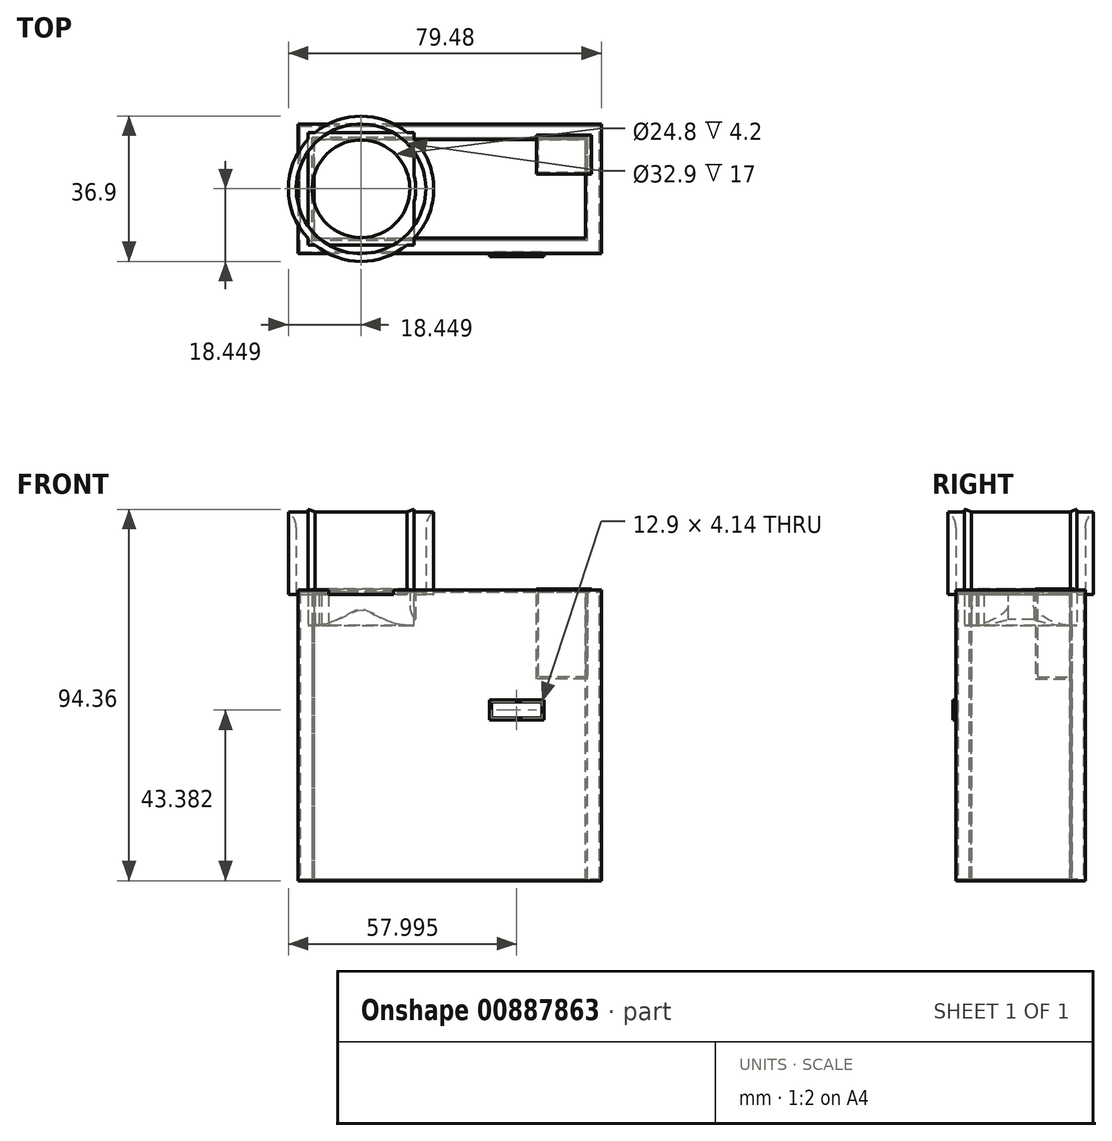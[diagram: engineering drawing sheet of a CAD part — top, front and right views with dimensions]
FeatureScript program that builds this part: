
annotation { "Feature Type Name" : "Feature", "Feature Type Description" : "" }
export const myFeature = defineFeature(function(context is Context, id is Id, definition is map)
    precondition{}
    {
        {
            var Q0;
            Q0=qCreatedBy(makeId("Front.planeOp"),FACE);
            var sketch = newSketch(context, id + "F0", { "sketchPlane" : qUnion([Q0])});
            skLineSegment(sketch, "E0", {"start": v(-38.5, 50.2) * mm, "end": v(38.5, 50.2) * mm});
            skLineSegment(sketch, "E1", {"start": v(-38.5, 50.2) * mm, "end": v(-38.5, -23.7) * mm});
            skLineSegment(sketch, "E2", {"start": v(-38.5, -23.7) * mm, "end": v(38.5, -23.7) * mm});
            skLineSegment(sketch, "E3", {"start": v(38.5, -23.7) * mm, "end": v(38.5, 50.2) * mm});
            skSolve(sketch);
        }
        {
            var Q0;
            Q0=makeQuery(id+"F0.imprint","IMPRINT",FACE,{"disambiguationData":[TD([[makeQuery(id+"F0.imprint","IMPRINT",EDGE,{"derivedFrom":sQuery(id+"F0.wireOp",EDGE,"E0")}),-1.0]])]});
            extrude(context, id + "F1", {"entities" : qUnion([Q0]), "depth" : 33 * mm, "offsetDistance" : 25 * mm});
        }
        {
            var Q0;
            Q0=makeQuery(id+"F1.opExtrude","SWEPT_FACE",FACE,{"disambiguationData":[OSD([sQuery(id+"F0.wireOp",EDGE,"E0")])]});
            var Q1;
            Q1=makeQuery(id+"F1.opExtrude","SWEPT_FACE",FACE,{"disambiguationData":[OSD([sQuery(id+"F0.wireOp",EDGE,"E2")])]});
            shell(context, id + "F2", {"entities" : qUnion([Q0, Q1]), "thickness" : 4 * mm});
        }
        {
            var Q0;
            Q0=qCreatedBy(makeId("Top.planeOp"),FACE);
            var sketch = newSketch(context, id + "F3", { "sketchPlane" : qUnion([Q0])});
            skLineSegment(sketch, "E4", {"start": v(35.98, -2.86) * mm, "end": v(21.98, -2.86) * mm});
            skLineSegment(sketch, "E5", {"start": v(21.98, -2.86) * mm, "end": v(21.98, -12.76) * mm});
            skLineSegment(sketch, "E6", {"start": v(21.98, -12.76) * mm, "end": v(35.98, -12.76) * mm});
            skLineSegment(sketch, "E7", {"start": v(35.98, -12.76) * mm, "end": v(35.98, -2.86) * mm});
            skSolve(sketch);
        }
        {
            var Q0;
            Q0=makeQuery(id+"F3.imprint","IMPRINT",FACE,{"disambiguationData":[TD([[makeQuery(id+"F3.imprint","IMPRINT",EDGE,{"derivedFrom":sQuery(id+"F3.wireOp",EDGE,"E4")}),1.0]])]});
            extrude(context, id + "F4", {"entities" : qUnion([Q0]), "operationType" : NewBodyOperationType.ADD, "depth" : 50.4 * mm, "offsetDistance" : 25 * mm, "hasSecondDirection" : true, "secondDirectionOppositeDirection" : false, "secondDirectionDepth" : 27.6 * mm});
        }
        {
            var Q0;
            Q0=qCreatedBy(makeId("Front.planeOp"),FACE);
            var sketch = newSketch(context, id + "F5", { "sketchPlane" : qUnion([Q0])});
            skLineSegment(sketch, "E8", {"start": v(10.07, 22.25) * mm, "end": v(10.07, 17.15) * mm});
            skLineSegment(sketch, "E9", {"start": v(10.07, 17.15) * mm, "end": v(23.97, 17.11) * mm});
            skLineSegment(sketch, "E10", {"start": v(10.07, 22.25) * mm, "end": v(23.97, 22.25) * mm});
            skLineSegment(sketch, "E11", {"start": v(23.97, 22.25) * mm, "end": v(23.97, 17.11) * mm});
            skPoint(sketch, "E12.end.orphan", {"position": v(23.97, 44.47) * mm});
            skLineSegment(sketch, "E13", {"start": v(49.26, 49.96) * mm, "end": v(49.26, 22.46) * mm});
            skSolve(sketch);
        }
        {
            var Q0;
            Q0 = qSketchRegion(id + "F5", true);
            extrude(context, id + "F6", {"entities" : qUnion([Q0]), "operationType" : NewBodyOperationType.ADD, "depth" : 33.7 * mm, "offsetDistance" : 25 * mm, "hasSecondDirection" : true, "secondDirectionOppositeDirection" : false, "secondDirectionDepth" : 30.4 * mm});
        }
        {
            var Q0;
            Q0=makeQuery(id+"F6.opExtrude","CAP_FACE",FACE,{"disambiguationData":[OSD([sQuery(id+"F5.wireOp",EDGE,"E8"),sQuery(id+"F5.wireOp",EDGE,"E9"),sQuery(id+"F5.wireOp",EDGE,"E10"),sQuery(id+"F5.wireOp",EDGE,"E11")])],"isStart":false});
            var Q1;
            Q1=makeQuery(id+"F6.opExtrude","CAP_FACE",FACE,{"disambiguationData":[OSD([sQuery(id+"F5.wireOp",EDGE,"E8"),sQuery(id+"F5.wireOp",EDGE,"E9"),sQuery(id+"F5.wireOp",EDGE,"E10"),sQuery(id+"F5.wireOp",EDGE,"E11")])],"isStart":true});
            shell(context, id + "F7", {"entities" : qUnion([Q0, Q1]), "thickness" : .5 * mm});
        }
        {
            var Q0;
            Q0=qCreatedBy(makeId("Top.planeOp"),FACE);
            var sketch = newSketch(context, id + "F8", { "sketchPlane" : qUnion([Q0])});
            skLineSegment(sketch, "E14", {"start": v(-36.03, -2.23) * mm, "end": v(-9.03, -2.23) * mm});
            skLineSegment(sketch, "E15", {"start": v(-9.03, -2.23) * mm, "end": v(-9.03, -30.73) * mm});
            skLineSegment(sketch, "E16", {"start": v(-9.03, -30.73) * mm, "end": v(-36.03, -30.73) * mm});
            skLineSegment(sketch, "E17", {"start": v(-36.03, -30.73) * mm, "end": v(-36.03, -2.23) * mm});
            skCircle(sketch, "E18", {"center": v(-22.53, -16.48) * mm, "radius": 12.4 * mm});
            skPoint(sketch, "E19.orphan", {"position": v(-22.53, -2.23) * mm});
            skPoint(sketch, "E20.start.orphan", {"position": v(-36.03, -16.48) * mm});
            skCircle(sketch, "E21.0", {"center": v(-22.53, -16.48) * mm, "radius": 13.9 * mm});
            skCircle(sketch, "E22", {"center": v(-22.53, -16.48) * mm, "radius": 16.45 * mm});
            skCircle(sketch, "E23.0", {"center": v(-22.53, -16.48) * mm, "radius": 18.45 * mm});
            skSolve(sketch);
        }
        {
            var Q0;
            Q0=makeQuery(id+"F8.imprint","IMPRINT",FACE,{"disambiguationData":[TD([[makeQuery(id+"F8.imprint","IMPRINT",EDGE,{"derivedFrom":sQuery(id+"F8.wireOp",EDGE,"E18")}),-1.0]])]});
            var Q1;
            {var subQ0=sQuery(id+"F8.wireOp",EDGE,"E14");Q1=makeQuery(id+"F8.imprint","IMPRINT",FACE,{"disambiguationData":[TD([[makeQuery(id+"F8.imprint","IMPRINT",EDGE,{"derivedFrom":subQ0}),-1.0]])]});}
            var Q2;
            {var subQ0=sQuery(id+"F8.wireOp",EDGE,"E16");Q2=makeQuery(id+"F8.imprint","IMPRINT",FACE,{"disambiguationData":[TD([[makeQuery(id+"F8.imprint","IMPRINT",EDGE,{"derivedFrom":subQ0}),-1.0]])]});}
            var Q3;
            {var subQ0=sQuery(id+"F8.wireOp",EDGE,"E21.0");var subQ1=sQuery(id+"F8.wireOp",EDGE,"E15");var subQ2=makeQuery(id+"F8.imprint","INTERSECT",VERTEX,{"disambiguationData":[OD(0.0)],"derivedFrom":[subQ1,subQ0]});Q3=makeQuery(id+"F8.imprint","IMPRINT",FACE,{"disambiguationData":[TD([[makeQuery(id+"F8.imprint","IMPRINT",EDGE,{"disambiguationData":[TD([[subQ2,-1.0]])],"derivedFrom":subQ1}),1.0]])]});}
            var Q4;
            {var subQ0=sQuery(id+"F8.wireOp",EDGE,"E21.0");var subQ1=sQuery(id+"F8.wireOp",EDGE,"E15");var subQ2=makeQuery(id+"F8.imprint","INTERSECT",VERTEX,{"disambiguationData":[OD(1.0)],"derivedFrom":[subQ1,subQ0]});Q4=makeQuery(id+"F8.imprint","IMPRINT",FACE,{"disambiguationData":[TD([[makeQuery(id+"F8.imprint","IMPRINT",EDGE,{"disambiguationData":[TD([[subQ2,-1.0]])],"derivedFrom":subQ1}),-1.0]])]});}
            var Q5;
            {var subQ5=sQuery(id+"F8.wireOp",EDGE,"E22");var subQ8=sQuery(id+"F8.wireOp",EDGE,"E14");var subQ10=makeQuery(id+"F8.imprint","INTERSECT",VERTEX,{"disambiguationData":[OD(0.0)],"derivedFrom":[subQ8,subQ5]});Q5=makeQuery(id+"F8.imprint","IMPRINT",FACE,{"disambiguationData":[TD([[makeQuery(id+"F8.imprint","IMPRINT",EDGE,{"disambiguationData":[TD([[subQ10,-1.0]])],"derivedFrom":subQ8}),-1.0]])]});}
            var Q6;
            {var subQ0=sQuery(id+"F8.wireOp",EDGE,"E23.0");var subQ1=sQuery(id+"F8.wireOp",EDGE,"E16");var subQ2=makeQuery(id+"F8.imprint","INTERSECT",VERTEX,{"disambiguationData":[OD(1.0)],"derivedFrom":[subQ1,subQ0]});Q6=makeQuery(id+"F8.imprint","IMPRINT",FACE,{"disambiguationData":[TD([[makeQuery(id+"F8.imprint","IMPRINT",EDGE,{"disambiguationData":[TD([[subQ2,1.0]])],"derivedFrom":subQ1}),-1.0]])]});}
            var Q7;
            {var subQ0=sQuery(id+"F8.wireOp",EDGE,"E23.0");var subQ1=sQuery(id+"F8.wireOp",EDGE,"E14");var subQ2=makeQuery(id+"F8.imprint","INTERSECT",VERTEX,{"disambiguationData":[OD(0.0)],"derivedFrom":[subQ1,subQ0]});Q7=makeQuery(id+"F8.imprint","IMPRINT",FACE,{"disambiguationData":[TD([[makeQuery(id+"F8.imprint","IMPRINT",EDGE,{"disambiguationData":[TD([[subQ2,-1.0]])],"derivedFrom":subQ1}),-1.0]])]});}
            var Q8;
            {var subQ0=sQuery(id+"F8.wireOp",EDGE,"E23.0");var subQ1=sQuery(id+"F8.wireOp",EDGE,"E15");var subQ2=makeQuery(id+"F8.imprint","INTERSECT",VERTEX,{"disambiguationData":[OD(1.0)],"derivedFrom":[subQ1,subQ0]});Q8=makeQuery(id+"F8.imprint","IMPRINT",FACE,{"disambiguationData":[TD([[makeQuery(id+"F8.imprint","IMPRINT",EDGE,{"disambiguationData":[TD([[subQ2,1.0]])],"derivedFrom":subQ1}),-1.0]])]});}
            var Q9;
            {var subQ0=sQuery(id+"F8.wireOp",EDGE,"E23.0");var subQ1=sQuery(id+"F8.wireOp",EDGE,"E14");var subQ2=makeQuery(id+"F8.imprint","INTERSECT",VERTEX,{"disambiguationData":[OD(1.0)],"derivedFrom":[subQ1,subQ0]});Q9=makeQuery(id+"F8.imprint","IMPRINT",FACE,{"disambiguationData":[TD([[makeQuery(id+"F8.imprint","IMPRINT",EDGE,{"disambiguationData":[TD([[subQ2,1.0]])],"derivedFrom":subQ1}),-1.0]])]});}
            extrude(context, id + "F9", {"entities" : qUnion([Q0, Q1, Q2, Q3, Q4, Q5, Q6, Q7, Q8, Q9]), "operationType" : NewBodyOperationType.ADD, "depth" : 50.4 * mm, "offsetDistance" : 25 * mm, "hasSecondDirection" : true, "secondDirectionOppositeDirection" : false, "secondDirectionDepth" : 41.2 * mm});
        }
        {
            var Q0;
            Q0 = qSketchRegion(id + "F8", true);
            extrude(context, id + "F10", {"entities" : qUnion([Q0]), "operationType" : NewBodyOperationType.ADD, "depth" : 71 * mm, "offsetDistance" : 25 * mm, "hasSecondDirection" : true, "secondDirectionOppositeDirection" : false, "secondDirectionDepth" : 49 * mm});
        }
        {
            var Q0;
            Q0=makeQuery(id+"F9.opExtrude","CAP_EDGE",EDGE,{"disambiguationData":[OSD([sQuery(id+"F8.wireOp",EDGE,"E18")])],"isStart":true});
            var Q1;
            Q1=makeQuery(id+"F10.opExtrude","CAP_EDGE",EDGE,{"disambiguationData":[OSD([sQuery(id+"F8.wireOp",EDGE,"E22")])],"isStart":false});
            fillet(context, id + "F11", {"entities" : qUnion([Q0, Q1]), "radius" : 5 * mm, "tangentPropagation" : true, "allowEdgeOverflow" : false});
        }
    });
